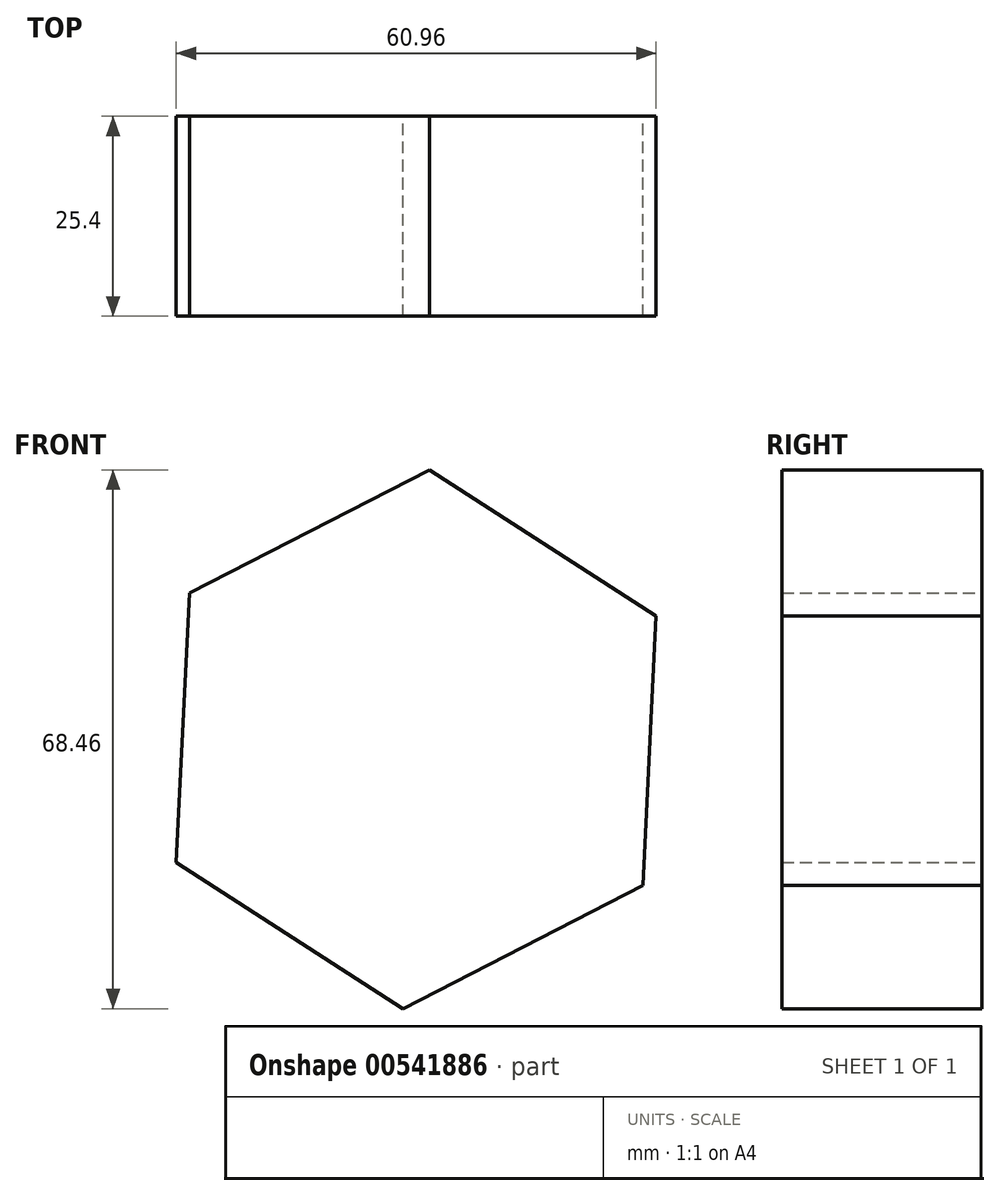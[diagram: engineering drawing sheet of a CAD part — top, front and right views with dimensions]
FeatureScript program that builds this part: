
annotation { "Feature Type Name" : "Feature", "Feature Type Description" : "" }
export const myFeature = defineFeature(function(context is Context, id is Id, definition is map)
    precondition{}
    {
        {
            var Q0;
            Q0=qCreatedBy(makeId("Front.planeOp"),FACE);
            var sketch = newSketch(context, id + "F0", { "sketchPlane" : qUnion([Q0])});
            skCircle(sketch, "E0.cCircle", {"center": v(0, 0) * mm, "radius": 29.68 * mm, "construction": true});
            skLineSegment(sketch, "E0.0", {"start": v(28.8, -18.56) * mm, "end": v(-1.68, -34.23) * mm});
            skLineSegment(sketch, "E0.1", {"start": v(-1.68, -34.23) * mm, "end": v(-30.48, -15.66) * mm});
            skLineSegment(sketch, "E0.2", {"start": v(-30.48, -15.66) * mm, "end": v(-28.8, 18.56) * mm});
            skLineSegment(sketch, "E0.3", {"start": v(-28.8, 18.56) * mm, "end": v(1.68, 34.23) * mm});
            skLineSegment(sketch, "E0.4", {"start": v(1.68, 34.23) * mm, "end": v(30.48, 15.66) * mm});
            skLineSegment(sketch, "E0.5", {"start": v(30.48, 15.66) * mm, "end": v(28.8, -18.56) * mm});
            skPoint(sketch, "E0.0.midPoint", {"position": v(13.56, -26.4) * mm});
            skSolve(sketch);
        }
        {
            var Q0;
            Q0 = qSketchRegion(id + "F0", true);
            extrude(context, id + "F1", {"entities" : qUnion([Q0]), "depth" : 25.4 * mm, "offsetDistance" : 25.4 * mm});
        }
        {
            var Q0;
            Q0=qCreatedBy(makeId("Front.planeOp"),FACE);
            var sketch = newSketch(context, id + "F2", { "sketchPlane" : qUnion([Q0])});
            skCircle(sketch, "E1", {"center": v(0, 0) * mm, "radius": 16.13 * mm});
            skSolve(sketch);
        }
        {
            var Q0;
            Q0 = qSketchRegion(id + "F2", true);
            extrude(context, id + "F3", {"entities" : qUnion([Q0]), "operationType" : NewBodyOperationType.ADD, "depth" : 25.4 * mm, "offsetDistance" : 25.4 * mm});
        }
    });
